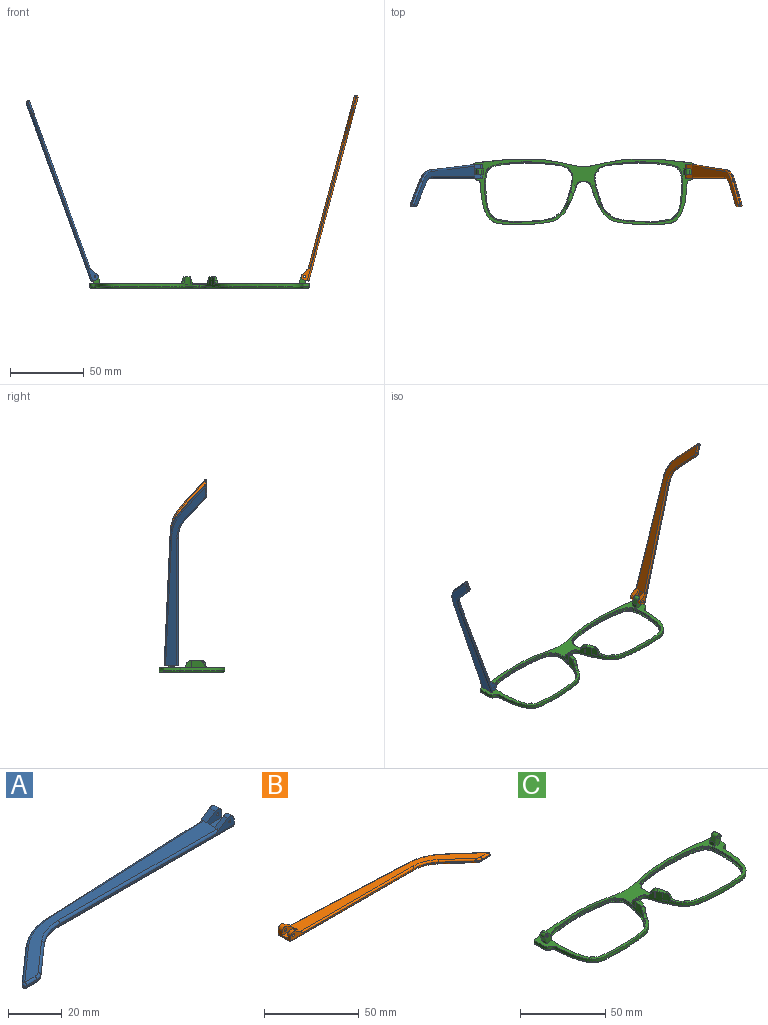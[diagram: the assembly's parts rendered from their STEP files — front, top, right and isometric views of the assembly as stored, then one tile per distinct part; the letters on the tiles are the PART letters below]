
ASSEMBLY  parts=3 mates=2
PART A: 43 faces, bbox 130.2x29.5x5.9 mm
  f0: plane 9.62x3.72mm, normal (1,0,0), area 24.7mm2, adj f1,f3,f4,f5,f10,f16,f18,f28
  f1: cylinder r=2.2mm len=3.45mm, axis (0,-1,0), area 11mm2, adj f0,f2,f4,f37
  f2: plane 6.01x3.91mm, normal (-0.55,0,0.84), area 12.7mm2, adj f1,f4,f9,f19,f37
  f3: plane 2.26x0.1mm, normal (0,0,1), area 0.1mm2, adj f0,f5,f18
  f4: plane 92.1x4.9mm, normal (0,-1,0), area 79.9mm2, adj f0,f1,f2,f14,f19,f36,f42
  f5: plane 93.42x4.13mm, normal (-0.04,1,0), area 64.8mm2, adj f0,f3,f11,f15,f17,f27,f28
  f6: plane 17.82x15.72mm, normal (-0.66,0.75,0), area 14.3mm2, adj f11,f12,f25,f30
  f7: plane 5.46x0.6mm, normal (0,-1,0), area 3.3mm2, adj f12,f13,f23,f32
  f8: plane 14.99x13.23mm, normal (0.66,-0.75,0), area 12mm2, adj f13,f14,f21,f34
  f9: plane 121.18x26.73mm, normal (0,0,1), area 627.7mm2, adj f2,f17,f19,f20,f21,f22,f23,f25
  f10: plane 129.1x27.08mm, normal (0,0,-1), area 686.5mm2, adj f0,f28,f29,f30,f32,f33,f34,f35
  f11: cylinder r=30mm len=18.52mm, axis (0,0,-1), area 12.2mm2, adj f5,f6,f26,f29
  f12: cylinder r=1mm len=1.75mm, axis (0,0,-1), area 1.5mm2, adj f6,f7,f24,f31
  f13: cylinder r=5mm len=3.31mm, axis (0,0,-1), area 2.2mm2, adj f7,f8,f22,f33
  f14: cylinder r=20mm len=13.23mm, axis (0,0,1), area 8.7mm2, adj f4,f8,f20,f35
  f15: plane 5.66x0.25mm, normal (0,0,-1), area 0.7mm2, adj f5,f17,f18
  f16: cylinder r=2.2mm len=3.45mm, axis (0,-1,0), area 14.8mm2, adj f0,f17,f18,f38
  f17: plane 6.01x3.91mm, normal (-0.55,0,0.84), area 16.9mm2, adj f5,f9,f15,f16,f18,f27,f38
  f18: plane 7.92x3.3mm, normal (0,1,0), area 15.9mm2, adj f0,f3,f15,f16,f17,f41
  f19: cylinder r=1mm len=84.18mm, axis (-1,0,0), area 131.4mm2, adj f2,f4,f9,f20
  f20: torus R=21mm, axis (0,0,1), area 23.1mm2, adj f9,f14,f19,f21
  f21: cylinder r=1mm len=15.65mm, axis (-0.75,-0.66,0), area 31.4mm2, adj f8,f9,f20,f22
  f22: torus R=4mm, axis (0,0,1), area 5.3mm2, adj f9,f13,f21,f23
  f23: cylinder r=1mm len=5.46mm, axis (-1,0,0), area 8.6mm2, adj f7,f9,f22,f24
  f24: sphere r=1mm, area 2.4mm2, adj f12,f23,f25
  f25: cylinder r=1mm len=18.48mm, axis (0.75,0.66,0), area 37.3mm2, adj f6,f9,f24,f26
  f26: torus R=29mm, axis (0,0,1), area 31.6mm2, adj f9,f11,f25,f27
  f27: cylinder r=1mm len=85.5mm, axis (1,0.04,0), area 133.5mm2, adj f5,f9,f17,f26
  f28: cylinder r=1mm len=93.46mm, axis (-1,-0.04,0), area 146.9mm2, adj f0,f5,f10,f29
  f29: torus R=29mm, axis (0,0,1), area 31.6mm2, adj f10,f11,f28,f30
  f30: cylinder r=1mm len=18.48mm, axis (-0.75,-0.66,0), area 37.3mm2, adj f6,f10,f29,f31
  f31: sphere r=1mm, area 2.4mm2, adj f12,f30,f32
  f32: cylinder r=1mm len=5.46mm, axis (1,0,0), area 8.6mm2, adj f7,f10,f31,f33
  f33: torus R=4mm, axis (0,0,1), area 5.3mm2, adj f10,f13,f32,f34
  f34: cylinder r=1mm len=15.65mm, axis (0.75,0.66,0), area 31.4mm2, adj f8,f10,f33,f35
  f35: torus R=21mm, axis (0,0,1), area 23.1mm2, adj f10,f14,f34,f36
  f36: cylinder r=1mm len=92.1mm, axis (1,0,0), area 144.7mm2, adj f0,f4,f10,f35
  f37: plane 7.92x4.7mm, normal (0,1,0), area 27mm2, adj f0,f1,f2,f39,f40,f42
  f38: plane 7.92x4.7mm, normal (0,-1,0), area 27mm2, adj f0,f16,f17,f39,f40,f41
  f39: plane 7.92x4.1mm, normal (0,0,1), area 32.5mm2, adj f0,f37,f38,f40
  f40: plane 4.1x1.4mm, normal (1,0,0), area 5.7mm2, adj f9,f37,f38,f39
  f41: cylinder r=0.5mm len=3.1mm, axis (0,-1,0), area 9.7mm2, adj f18,f38
  f42: cylinder r=0.5mm len=2.3mm, axis (0,-1,0), area 7.2mm2, adj f4,f37
PART B: 43 faces, bbox 130.2x29.5x5.9 mm
  f0: plane 9.62x3.72mm, normal (-1,0,0), area 24.7mm2, adj f1,f3,f4,f5,f10,f16,f18,f28
  f1: cylinder r=2.2mm len=3.45mm, axis (0,-1,0), area 11mm2, adj f0,f2,f4,f37
  f2: plane 6.01x3.91mm, normal (0.55,0,0.84), area 12.7mm2, adj f1,f4,f9,f19,f37
  f3: plane 2.26x0.1mm, normal (0,0,1), area 0.1mm2, adj f0,f5,f18
  f4: plane 92.1x4.9mm, normal (0,-1,0), area 78.2mm2, adj f0,f1,f2,f14,f19,f36,f42
  f5: plane 93.42x4.13mm, normal (0.04,1,0), area 64.8mm2, adj f0,f3,f11,f15,f17,f27,f28
  f6: plane 17.82x15.72mm, normal (0.66,0.75,0), area 14.3mm2, adj f11,f12,f25,f30
  f7: plane 5.46x0.6mm, normal (0,-1,0), area 3.3mm2, adj f12,f13,f23,f32
  f8: plane 14.99x13.23mm, normal (-0.66,-0.75,0), area 12mm2, adj f13,f14,f21,f34
  f9: plane 121.18x26.73mm, normal (0,0,1), area 627.7mm2, adj f2,f17,f19,f20,f21,f22,f23,f25
  f10: plane 129.1x27.08mm, normal (0,0,-1), area 686.5mm2, adj f0,f28,f29,f30,f32,f33,f34,f35
  f11: cylinder r=30mm len=18.52mm, axis (0,0,-1), area 12.2mm2, adj f5,f6,f26,f29
  f12: cylinder r=1mm len=1.75mm, axis (0,0,-1), area 1.5mm2, adj f6,f7,f24,f31
  f13: cylinder r=5mm len=3.31mm, axis (0,0,-1), area 2.2mm2, adj f7,f8,f22,f33
  f14: cylinder r=20mm len=13.23mm, axis (0,0,1), area 8.7mm2, adj f4,f8,f20,f35
  f15: plane 5.66x0.25mm, normal (0,0,-1), area 0.7mm2, adj f5,f17,f18
  f16: cylinder r=2.2mm len=3.45mm, axis (0,-1,0), area 14.8mm2, adj f0,f17,f18,f38
  f17: plane 6.01x3.91mm, normal (0.55,0,0.84), area 16.9mm2, adj f5,f9,f15,f16,f18,f27,f38
  f18: plane 7.92x3.3mm, normal (0,1,0), area 14.3mm2, adj f0,f3,f15,f16,f17,f41
  f19: cylinder r=1mm len=84.18mm, axis (1,0,0), area 131.4mm2, adj f2,f4,f9,f20
  f20: torus R=21mm, axis (0,0,1), area 23.1mm2, adj f9,f14,f19,f21
  f21: cylinder r=1mm len=15.65mm, axis (0.75,-0.66,0), area 31.4mm2, adj f8,f9,f20,f22
  f22: torus R=4mm, axis (0,0,1), area 5.3mm2, adj f9,f13,f21,f23
  f23: cylinder r=1mm len=5.46mm, axis (1,0,0), area 8.6mm2, adj f7,f9,f22,f24
  f24: sphere r=1mm, area 2.4mm2, adj f12,f23,f25
  f25: cylinder r=1mm len=18.48mm, axis (-0.75,0.66,0), area 37.3mm2, adj f6,f9,f24,f26
  f26: torus R=29mm, axis (0,0,1), area 31.6mm2, adj f9,f11,f25,f27
  f27: cylinder r=1mm len=85.5mm, axis (-1,0.04,0), area 133.5mm2, adj f5,f9,f17,f26
  f28: cylinder r=1mm len=93.46mm, axis (1,-0.04,0), area 146.9mm2, adj f0,f5,f10,f29
  f29: torus R=29mm, axis (0,0,1), area 31.6mm2, adj f10,f11,f28,f30
  f30: cylinder r=1mm len=18.48mm, axis (0.75,-0.66,0), area 37.3mm2, adj f6,f10,f29,f31
  f31: sphere r=1mm, area 2.4mm2, adj f12,f30,f32
  f32: cylinder r=1mm len=5.46mm, axis (-1,0,0), area 8.6mm2, adj f7,f10,f31,f33
  f33: torus R=4mm, axis (0,0,1), area 5.3mm2, adj f10,f13,f32,f34
  f34: cylinder r=1mm len=15.65mm, axis (-0.75,0.66,0), area 31.4mm2, adj f8,f10,f33,f35
  f35: torus R=21mm, axis (0,0,1), area 23.1mm2, adj f10,f14,f34,f36
  f36: cylinder r=1mm len=92.1mm, axis (-1,0,0), area 144.7mm2, adj f0,f4,f10,f35
  f37: plane 7.92x4.7mm, normal (0,1,0), area 25.4mm2, adj f0,f1,f2,f39,f40,f42
  f38: plane 7.92x4.7mm, normal (0,-1,0), area 25.4mm2, adj f0,f16,f17,f39,f40,f41
  f39: plane 7.92x4.1mm, normal (0,0,1), area 32.5mm2, adj f0,f37,f38,f40
  f40: plane 4.1x1.4mm, normal (-1,0,0), area 5.7mm2, adj f9,f37,f38,f39
  f41: cylinder r=0.88mm len=3.1mm, axis (0,-1,0), area 17mm2, adj f18,f38
  f42: cylinder r=0.88mm len=2.3mm, axis (0,-1,0), area 12.6mm2, adj f4,f37
PART C: 82 faces, bbox 149.3x44.8x11.3 mm
  f0: plane 4.36x1.05mm, normal (0,0,1), area 0.5mm2, adj f7,f26
  f1: plane 149.24x44.75mm, normal (0,0,1), area 910.4mm2, adj f2,f3,f7,f13,f14,f15,f16,f29
  f2: extruded ~74.52x44.62mm, area 344.5mm2, adj f1,f3,f8,f9,f10,f24,f25,f27
  f3: extruded ~36.97x5.09mm, area 74.8mm2, adj f1,f2,f11,f44
  f4: plane 147.24x42.64mm, normal (0,0,-1), area 535.6mm2, adj f8,f10,f11,f12,f48,f50,f51,f52
  f5: plane 60.23x41.4mm, normal (0,0,1), area 109.2mm2, adj f6,f12
  f6: extruded ~59.96x41.03mm, area 181.5mm2, adj f5,f7
  f7: extruded ~59.96x41.03mm, area 228mm2, adj f0,f1,f6,f26,f28,f30,f31,f32
  f8: bspline ~74.99x41.54mm, area 188.3mm2, adj f2,f4,f9,f48
  f9: bspline ~1.02x1mm, area 0.8mm2, adj f2,f8,f10
  f10: bspline ~38.83x3.68mm, area 58.1mm2, adj f2,f4,f9,f11
  f11: bspline ~46.84x6.1mm, area 58.8mm2, adj f3,f4,f10,f51
  f12: bspline ~60.75x41.95mm, area 268.5mm2, adj f4,f5
  f13: plane 7.01x5.32mm, normal (0,1,0), area 25.3mm2, adj f1,f14,f16,f17,f18,f19,f20,f21
  f14: plane 4x2.46mm, normal (-1,0,0), area 9.8mm2, adj f1,f13,f15,f17
  f15: plane 7.01x5.32mm, normal (0,-1,0), area 25.3mm2, adj f1,f14,f16,f17,f18,f19,f20,f21
  f16: plane 4x1mm, normal (1,0,0), area 4mm2, adj f1,f13,f15,f19
  f17: plane 4x0.17mm, normal (0.34,0,0.94), area 0.7mm2, adj f13,f14,f15,f18
  f18: plane 4x3.31mm, normal (-0.94,0,0.34), area 14.1mm2, adj f13,f15,f17,f21
  f19: plane 4x3.31mm, normal (0.94,0,-0.34), area 14.1mm2, adj f13,f15,f16,f22
  f20: plane 4x0.11mm, normal (0.34,0,0.94), area 0.5mm2, adj f13,f15,f21,f22
  f21: cylinder r=1.98mm len=4mm, axis (0,1,0), area 12.4mm2, adj f13,f15,f18,f20
  f22: cylinder r=1.98mm len=4mm, axis (0,-1,0), area 12.4mm2, adj f13,f15,f19,f20
  f23: cylinder r=0.88mm len=4mm, axis (0,-1,0), area 22mm2, adj f13,f15
  f24: extruded ~4.78x0.54mm, area 2.7mm2, adj f2,f29
  f25: extruded ~5.3x4.19mm, area 22.5mm2, adj f2,f28,f30,f39,f41
  f26: extruded ~5x4.27mm, area 16.4mm2, adj f0,f7,f28,f29
  f27: extruded ~0.32x0.15mm, area 0mm2, adj f2,f29
  f28: plane 8.19x3.71mm, normal (0,0,1), area 14.7mm2, adj f2,f7,f25,f26,f29,f30
  f29: bspline ~12.39x9.19mm, area 23mm2, adj f1,f2,f24,f26,f27,f28,f40
  f30: bspline ~7.27x7.27mm, area 9.1mm2, adj f7,f25,f28,f39
  f31: plane 2.81x2.1mm, normal (0,0,-1), area 2.2mm2, adj f7,f32
  f32: cylinder r=2.28mm len=2.76mm, axis (0,0,1), area 1.9mm2, adj f1,f7,f31
  f33: plane 2.48x2.29mm, normal (0,0,-1), area 2.2mm2, adj f7,f34
  f34: cylinder r=2.28mm len=2.45mm, axis (0,0,1), area 1.9mm2, adj f1,f7,f33
  f35: plane 2.16x1.89mm, normal (0,0,-1), area 2.1mm2, adj f7,f36
  f36: cylinder r=1.3mm len=2.15mm, axis (0,0,1), area 1.8mm2, adj f1,f7,f35
  f37: plane 1.94x1.87mm, normal (0,0,-1), area 1.8mm2, adj f7,f38
  f38: cylinder r=1.3mm len=1.93mm, axis (0,0,1), area 1.6mm2, adj f1,f7,f37
  f39: bspline ~4.01x3.8mm, area 7.4mm2, adj f1,f2,f7,f25,f30
  f40: bspline ~6.26x4.6mm, area 3.1mm2, adj f1,f2,f29,f80
  f41: bspline ~5.09x2.57mm, area 0mm2, adj f2,f25
  f42: plane 4.36x1.05mm, normal (0,0,1), area 0.5mm2, adj f47,f66
  f43: extruded ~74.52x44.62mm, area 344.6mm2, adj f1,f2,f44,f48,f49,f50,f64,f65
  f44: extruded ~36.97x5.09mm, area 74.8mm2, adj f1,f3,f43,f51
  f45: plane 60.23x41.4mm, normal (0,0,1), area 109.2mm2, adj f46,f52
  f46: extruded ~59.96x41.03mm, area 181.5mm2, adj f45,f47
  f47: extruded ~59.96x41.03mm, area 228mm2, adj f1,f42,f46,f66,f68,f70,f71,f72
  f48: bspline ~74.99x41.54mm, area 188.3mm2, adj f4,f8,f43,f49
  f49: bspline ~1.02x1mm, area 0.7mm2, adj f43,f48,f50
  f50: bspline ~38.75x3.65mm, area 58.1mm2, adj f4,f43,f49,f51
  f51: bspline ~46.84x6.1mm, area 58.8mm2, adj f4,f11,f44,f50
  f52: bspline ~60.74x41.95mm, area 268.5mm2, adj f4,f45
  f53: plane 7.01x5.32mm, normal (0,1,0), area 25.3mm2, adj f1,f54,f56,f57,f58,f59,f60,f61
  f54: plane 4x2.46mm, normal (1,0,0), area 9.8mm2, adj f1,f53,f55,f57
  f55: plane 7.01x5.32mm, normal (0,-1,0), area 25.3mm2, adj f1,f54,f56,f57,f58,f59,f60,f61
  f56: plane 4x1mm, normal (-1,0,0), area 4mm2, adj f1,f53,f55,f59
  f57: plane 4x0.17mm, normal (-0.34,0,0.94), area 0.7mm2, adj f53,f54,f55,f58
  f58: plane 4x3.31mm, normal (0.94,0,0.34), area 14.1mm2, adj f53,f55,f57,f61
  f59: plane 4x3.31mm, normal (-0.94,0,-0.34), area 14.1mm2, adj f53,f55,f56,f62
  f60: plane 4x0.11mm, normal (-0.34,0,0.94), area 0.5mm2, adj f53,f55,f61,f62
  f61: cylinder r=1.98mm len=4mm, axis (0,1,0), area 12.4mm2, adj f53,f55,f58,f60
  f62: cylinder r=1.98mm len=4mm, axis (0,-1,0), area 12.4mm2, adj f53,f55,f59,f60
  f63: cylinder r=0.88mm len=4mm, axis (0,-1,0), area 22mm2, adj f53,f55
  f64: extruded ~4.78x0.54mm, area 2.7mm2, adj f43,f69
  f65: extruded ~5.3x4.19mm, area 22.5mm2, adj f43,f68,f70,f79,f81
  f66: extruded ~5x4.27mm, area 16.4mm2, adj f42,f47,f68,f69
  f67: extruded ~0.32x0.15mm, area 0mm2, adj f43,f69
  f68: plane 8.19x3.71mm, normal (0,0,1), area 14.7mm2, adj f43,f47,f65,f66,f69,f70
  f69: bspline ~12.39x9.19mm, area 23mm2, adj f1,f43,f64,f66,f67,f68,f80
  f70: bspline ~7.27x7.27mm, area 9.1mm2, adj f47,f65,f68,f79
  f71: plane 2.81x2.1mm, normal (0,0,-1), area 2.2mm2, adj f47,f72
  f72: cylinder r=2.28mm len=2.76mm, axis (0,0,1), area 1.9mm2, adj f1,f47,f71
  f73: plane 2.48x2.29mm, normal (0,0,-1), area 2.2mm2, adj f47,f74
  f74: cylinder r=2.28mm len=2.45mm, axis (0,0,1), area 1.9mm2, adj f1,f47,f73
  f75: plane 2.16x1.89mm, normal (0,0,-1), area 2.1mm2, adj f47,f76
  f76: cylinder r=1.3mm len=2.15mm, axis (0,0,1), area 1.8mm2, adj f1,f47,f75
  f77: plane 1.94x1.87mm, normal (0,0,-1), area 1.8mm2, adj f47,f78
  f78: cylinder r=1.3mm len=1.93mm, axis (0,0,1), area 1.6mm2, adj f1,f47,f77
  f79: bspline ~4.01x3.8mm, area 7.4mm2, adj f1,f43,f47,f65,f70
  f80: bspline ~6.26x4.6mm, area 3.1mm2, adj f1,f40,f43,f69
  f81: bspline ~5.09x2.57mm, area 0mm2, adj f43,f65
PLACE A rot(axis=(0,1,0),70deg) t=(-84.97,-5.75,56.04)mm
PLACE B rot(axis=(0,-1,0),75deg) t=(68.2,-5.75,-61.61)mm
PLACE C t=(10,-9.92,-5.77)mm
MATE revolute A.f1 <-> C.f61  axis (0,-1,0) through (-61.09,2.72,1.25)mm
MATE revolute B.f41 <-> C.f22  axis (0,-1,0) through (81.2,2.72,1.21)mm
